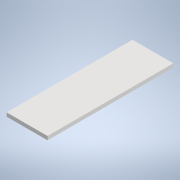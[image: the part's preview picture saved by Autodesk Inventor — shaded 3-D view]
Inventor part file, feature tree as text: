
AUTODESK INVENTOR PART (.ipt)
format: ipt  version: 2021 (Build 250183000, 183)  size: 90,624 bytes
history: native  units: in
note: dims shown in document units (in); Inventor stores cm internally (conversion verified against a paired STEP export)
features: other x3, extrude x1, sketch x1, reference x1
ambient origin geometry x8: Origin, YZ Plane, XZ Plane, XY Plane, X Axis, Y Axis, Z Axis, Center Point
bodies: Solid1 (feature_tree)
feature tree (6):
  extrude  "Extrusion1"  [1 undecoded]
  sketch  "Sketch1"  dims[d2=16.9291in d3=0.0in]
  reference  "Reference1"
  other  "<userpath>\Documents\Inventor CAD\Kerbal Kontroller\v.2.iam"
  other  "v.2.iam"
  other  "Side:1"
note: 1 required parameter value undecoded (feature->parameter linkage not recoverable at this tier; creation-order binding heuristic only, values carry confidence <= 0.55)
